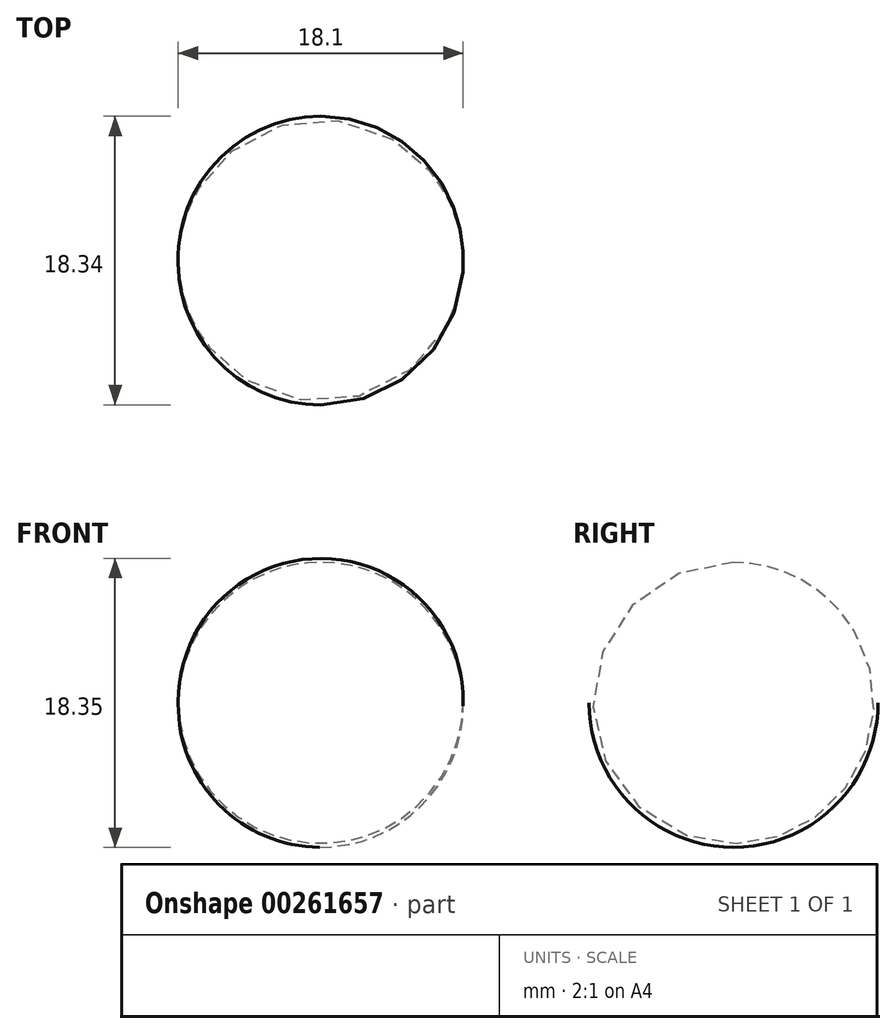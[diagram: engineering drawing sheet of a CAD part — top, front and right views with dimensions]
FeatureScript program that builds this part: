
annotation { "Feature Type Name" : "Feature", "Feature Type Description" : "" }
export const myFeature = defineFeature(function(context is Context, id is Id, definition is map)
    precondition{}
    {
        {
            var Q0;
            Q0=qCreatedBy(makeId("Front.planeOp"),FACE);
            var sketch = newSketch(context, id + "F0", { "sketchPlane" : qUnion([Q0])});
            skArc(sketch, "E0", {"start": v(59.19, 52.3) * mm, "mid": v(50.2, 61.54) * mm, "end": v(41.09, 52.43) * mm});
            skLineSegment(sketch, "E1", {"start": v(59.19, 52.3) * mm, "end": v(41.09, 52.43) * mm});
            skPoint(sketch, "E2.orphan", {"position": v(32.62, 52.49) * mm});
            skSolve(sketch);
        }
        {
            var Q0;
            Q0=makeQuery(id+"F0.imprint","IMPRINT",FACE,{"disambiguationData":[TD([[makeQuery(id+"F0.imprint","IMPRINT",EDGE,{"derivedFrom":sQuery(id+"F0.wireOp",EDGE,"E0")}),1.0]])]});
            var Q1;
            Q1=sQuery(id+"F0.wireOp",EDGE,"E1");
            revolve(context, id + "F1", {"entities" : qUnion([Q0]), "axis" : qUnion([Q1]), "revolveType" : RevolveType.FULL});
        }
    });
